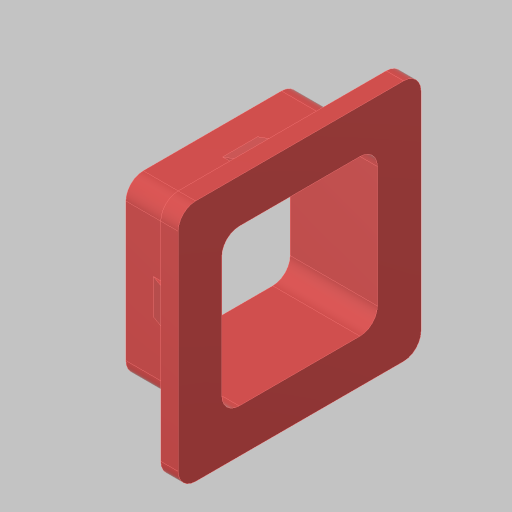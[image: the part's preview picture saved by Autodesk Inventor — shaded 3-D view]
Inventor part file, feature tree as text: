
AUTODESK INVENTOR PART (.ipt)
format: ipt  version: 2023.5 (Build 275446000, 446)  size: 163,840 bytes
history: native  units: in
note: dims shown in document units (in); Inventor stores cm internally (conversion verified against a paired STEP export)
features: extrude x3, sketch x3, fillet x1, pattern_circular x1, projected_geometry x1
ambient origin geometry x8: Origin, YZ Plane, XZ Plane, XY Plane, X Axis, Y Axis, Z Axis, Center Point
bodies: Solid1 (feature_tree)
feature tree (9):
  extrude  "Extrusion1"  Depth=1.24in
  extrude  "Extrusion2"  Depth=0.5in TaperAngle=0.0deg
  fillet  "Fillet1"  Radius=0.25in
  extrude  "Extrusion3"  Depth=0.125in
  pattern_circular  "Circular Pattern1"  [2 undecoded]
  sketch  "Sketch1"  dims[d0=1.24in d1=1.24in]
  sketch  "Sketch2"  dims[d2=0.0625in d3=0.5in d4=0.0in d5=0.25in]
  projected_geometry  "Projected Loop1"
  sketch  "Sketch4"  dims[d6=0.125in d7=0.0in d8=0.125in d9=0.13in d10=0.0625in d11=0.1374in d12=0.25in d13=0.0in d14=1.5748in d15=360.0deg]
note: 2 required parameter values undecoded (feature->parameter linkage not recoverable at this tier; creation-order binding heuristic only, values carry confidence <= 0.55)
